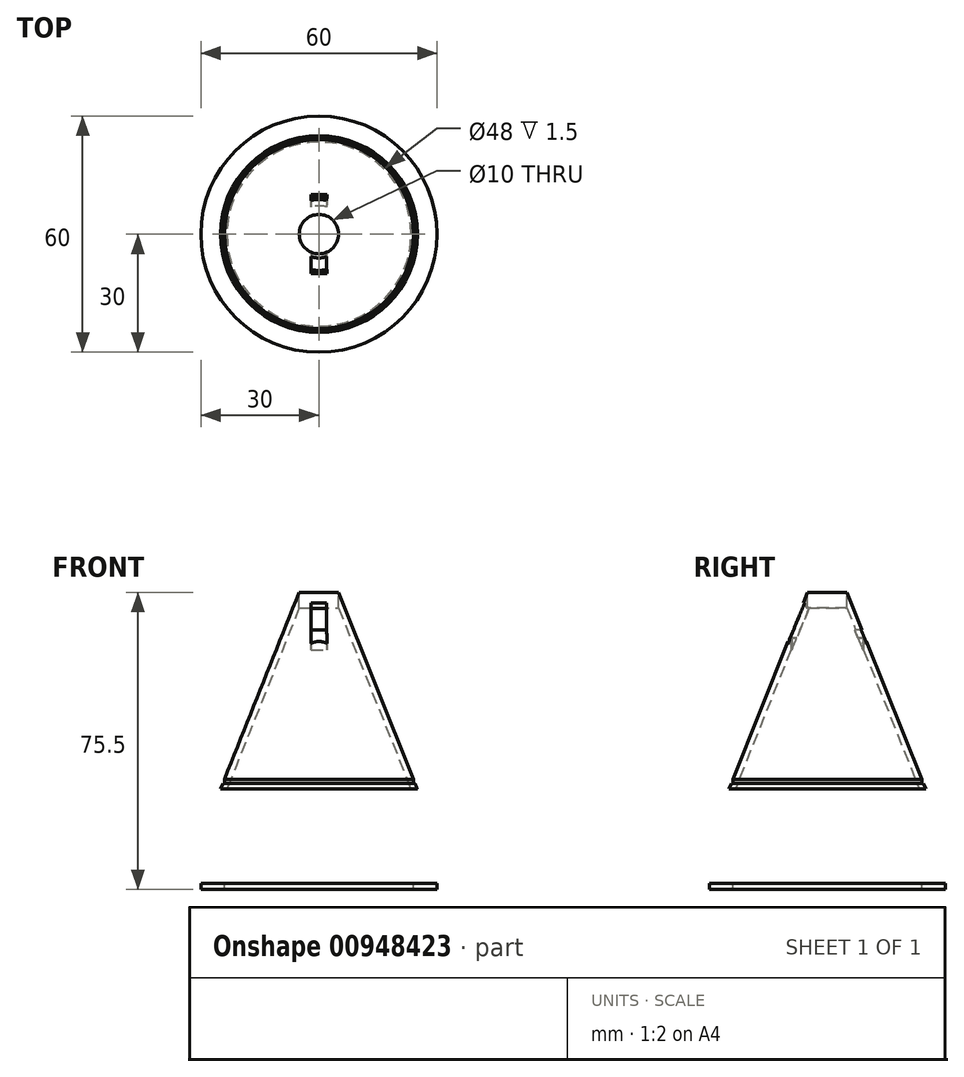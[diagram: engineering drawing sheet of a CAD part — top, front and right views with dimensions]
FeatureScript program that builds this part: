
annotation { "Feature Type Name" : "Feature", "Feature Type Description" : "" }
export const myFeature = defineFeature(function(context is Context, id is Id, definition is map)
    precondition{}
    {
        {
            var Q0;
            Q0=qCreatedBy(makeId("Front.planeOp"),FACE);
            var sketch = newSketch(context, id + "F0", { "sketchPlane" : qUnion([Q0])});
            skLineSegment(sketch, "E0", {"start": v(0, 0) * mm, "end": v(0, 25) * mm});
            skLineSegment(sketch, "E1", {"start": v(0, 25) * mm, "end": v(0, -25) * mm});
            skLineSegment(sketch, "E2", {"start": v(0, -25) * mm, "end": v(-25, -25) * mm});
            skLineSegment(sketch, "E3", {"start": v(0, 25) * mm, "end": v(-5, 25) * mm});
            skLineSegment(sketch, "E4", {"start": v(-5, 25) * mm, "end": v(-25, -25) * mm});
            skSolve(sketch);
        }
        {
            var Q0;
            {var subQ2=sQuery(id+"F0.wireOp",EDGE,"E2");Q0=makeQuery(id+"F0.imprint","IMPRINT",FACE,{"disambiguationData":[TD([[makeQuery(id+"F0.imprint","IMPRINT",EDGE,{"derivedFrom":subQ2}),-1.0]])]});}
            var Q1;
            Q1=sQuery(id+"F0.wireOp",EDGE,"E1");
            revolve(context, id + "F1", {"surfaceOperationType" : NewSurfaceOperationType.NEW, "entities" : qUnion([Q0]), "axis" : qUnion([Q1]), "revolveType" : RevolveType.FULL});
        }
        {
            var Q0;
            Q0=makeQuery(id+"F1.opRevolve","SWEPT_FACE",FACE,{"disambiguationData":[OSD([sQuery(id+"F0.wireOp",EDGE,"E2")])]});
            shell(context, id + "F2", {"entities" : qUnion([Q0]), "thickness" : 1.5 * mm});
        }
        {
            var Q0;
            Q0=makeQuery(id+"F1.opRevolve","SWEPT_FACE",FACE,{"disambiguationData":[OSD([sQuery(id+"F0.wireOp",EDGE,"E3")])]});
            extrude(context, id + "F3", {"entities" : qUnion([Q0]), "operationType" : NewBodyOperationType.REMOVE, "oppositeDirection" : true, "depth" : 25 * mm, "offsetDistance" : 25 * mm});
        }
        {
            var Q0;
            Q0=qCreatedBy(makeId("Top.planeOp"),FACE);
            var sketch = newSketch(context, id + "F4", { "sketchPlane" : qUnion([Q0])});
            skCircle(sketch, "E5", {"center": v(0, 0) * mm, "radius": 30 * mm});
            skCircle(sketch, "E6", {"center": v(0, 0) * mm, "radius": 24 * mm});
            skSolve(sketch);
        }
        {
            var Q0;
            Q0=makeQuery(id+"F4.imprint","IMPRINT",FACE,{"disambiguationData":[TD([[makeQuery(id+"F4.imprint","IMPRINT",EDGE,{"derivedFrom":sQuery(id+"F4.wireOp",EDGE,"E5")}),1.0]])]});
            extrude(context, id + "F5", {"entities" : qUnion([Q0]), "oppositeDirection" : true, "depth" : 25 * mm, "offsetDistance" : 25 * mm});
        }
        {
            var Q0;
            Q0=makeQuery(id+"F5.opExtrude","CAP_FACE",FACE,{"disambiguationData":[OSD([sQuery(id+"F4.wireOp",EDGE,"E5"),sQuery(id+"F4.wireOp",EDGE,"E6")])],"isStart":true});
            extrude(context, id + "F6", {"entities" : qUnion([Q0]), "operationType" : NewBodyOperationType.REMOVE, "oppositeDirection" : true, "depth" : 23.5 * mm, "offsetDistance" : 25 * mm});
        }
        {
            var Q0;
            Q0=qCreatedBy(makeId("Front.planeOp"),FACE);
            var sketch = newSketch(context, id + "F7", { "sketchPlane" : qUnion([Q0])});
            skLineSegment(sketch, "E7", {"start": v(0.03, 10.4) * mm, "end": v(2.03, 10.4) * mm});
            skLineSegment(sketch, "E8", {"start": v(0.03, 10.4) * mm, "end": v(-1.97, 10.4) * mm});
            skLineSegment(sketch, "E9", {"start": v(-1.97, 10.4) * mm, "end": v(-1.97, 15.5) * mm});
            skLineSegment(sketch, "E10", {"start": v(-1.97, 15.5) * mm, "end": v(2, 15.5) * mm});
            skLineSegment(sketch, "E11", {"start": v(2, 15.5) * mm, "end": v(2.03, 10.4) * mm});
            skSolve(sketch);
        }
        {
            var Q0;
            Q0 = qSketchRegion(id + "F7", true);
            extrude(context, id + "F8", {"entities" : qUnion([Q0]), "operationType" : NewBodyOperationType.ADD, "oppositeDirection" : true, "depth" : 10 * mm, "offsetDistance" : 25 * mm, "hasSecondDirection" : true, "secondDirectionOppositeDirection" : false, "secondDirectionDepth" : 10 * mm});
        }
        {
            var Q0;
            Q0=makeQuery(id+"F8.opExtrude","CAP_FACE",FACE,{"disambiguationData":[OSD([sQuery(id+"F7.wireOp",EDGE,"E7"),sQuery(id+"F7.wireOp",EDGE,"E8"),sQuery(id+"F7.wireOp",EDGE,"E9"),sQuery(id+"F7.wireOp",EDGE,"E10"),sQuery(id+"F7.wireOp",EDGE,"E11")])],"isStart":true});
            extrude(context, id + "F9", {"entities" : qUnion([Q0]), "operationType" : NewBodyOperationType.REMOVE, "endBound" : BoundingType.THROUGH_ALL, "oppositeDirection" : true, "depth" : 25 * mm, "offsetDistance" : 25 * mm});
        }
        {
            var Q0;
            Q0=makeQuery(id+"F8.opExtrude","SWEPT_FACE",FACE,{"disambiguationData":[OSD([sQuery(id+"F7.wireOp",EDGE,"E7"),sQuery(id+"F7.wireOp",EDGE,"E8")])]});
            extrude(context, id + "F10", {"entities" : qUnion([Q0]), "operationType" : NewBodyOperationType.REMOVE, "oppositeDirection" : true, "depth" : 3 * mm, "offsetDistance" : 25 * mm});
        }
        {
            var Q0;
            Q0=makeQuery(id+"F8.boolean.opBoolean","INTERSECT",EDGE,{"disambiguationData":[OD(1.0)],"derivedFrom":[makeQuery(id+"F1.opRevolve","SWEPT_FACE",FACE,{"disambiguationData":[OSD([sQuery(id+"F0.wireOp",EDGE,"E4")])]}),makeQuery(id+"F8.opExtrude","SWEPT_FACE",FACE,{"disambiguationData":[OSD([sQuery(id+"F7.wireOp",EDGE,"E10")])]})]});
            var Q1;
            Q1=makeQuery(id+"F8.boolean.opBoolean","INTERSECT",EDGE,{"disambiguationData":[OD(0.0)],"derivedFrom":[makeQuery(id+"F1.opRevolve","SWEPT_FACE",FACE,{"disambiguationData":[OSD([sQuery(id+"F0.wireOp",EDGE,"E4")])]}),makeQuery(id+"F8.opExtrude","SWEPT_FACE",FACE,{"disambiguationData":[OSD([sQuery(id+"F7.wireOp",EDGE,"E10")])]})]});
            chamfer(context, id + "F11", {"entities" : qUnion([Q0, Q1]), "width" : 5 * mm, "tangentPropagation" : true});
        }
        {
            var Q0;
            Q0=makeQuery(id+"F1.opRevolve","SWEPT_BODY",BODY,{"disambiguationData":[OSD([sQuery(id+"F0.wireOp",EDGE,"E1"),sQuery(id+"F0.wireOp",EDGE,"E2"),sQuery(id+"F0.wireOp",EDGE,"E3"),sQuery(id+"F0.wireOp",EDGE,"E4")])]});
            transform(context, id + "F12", {"entities" : qUnion([Q0]), "transformType" : TransformType.TRANSLATION_3D, "dx" : 0 * mm, "dy" : 0 * mm, "dz" : 24.5 * mm, "makeCopy" : true});
        }
        {
            var Q0;
            Q0=makeQuery(id+"F12.opPattern","COPY",BODY,{"derivedFrom":makeQuery(id+"F1.opRevolve","SWEPT_BODY",BODY,{"disambiguationData":[OSD([sQuery(id+"F0.wireOp",EDGE,"E1"),sQuery(id+"F0.wireOp",EDGE,"E2"),sQuery(id+"F0.wireOp",EDGE,"E3"),sQuery(id+"F0.wireOp",EDGE,"E4")])]}),"instanceName":"1"});
            deleteBodies(context, id + "F13", {"entities" : qUnion([Q0])});
        }
        {
            var Q0;
            Q0=makeQuery(id+"F1.opRevolve","SWEPT_BODY",BODY,{"disambiguationData":[OSD([sQuery(id+"F0.wireOp",EDGE,"E1"),sQuery(id+"F0.wireOp",EDGE,"E2"),sQuery(id+"F0.wireOp",EDGE,"E3"),sQuery(id+"F0.wireOp",EDGE,"E4")])]});
            transform(context, id + "F14", {"entities" : qUnion([Q0]), "transformType" : TransformType.TRANSLATION_3D, "dx" : 0 * mm, "dy" : 0 * mm, "dz" : 25.5 * mm, "makeCopy" : true});
        }
        {
            var Q0;
            Q0=makeQuery(id+"F1.opRevolve","SWEPT_BODY",BODY,{"disambiguationData":[OSD([sQuery(id+"F0.wireOp",EDGE,"E1"),sQuery(id+"F0.wireOp",EDGE,"E2"),sQuery(id+"F0.wireOp",EDGE,"E3"),sQuery(id+"F0.wireOp",EDGE,"E4")])]});
            deleteBodies(context, id + "F15", {"entities" : qUnion([Q0])});
        }
    });
